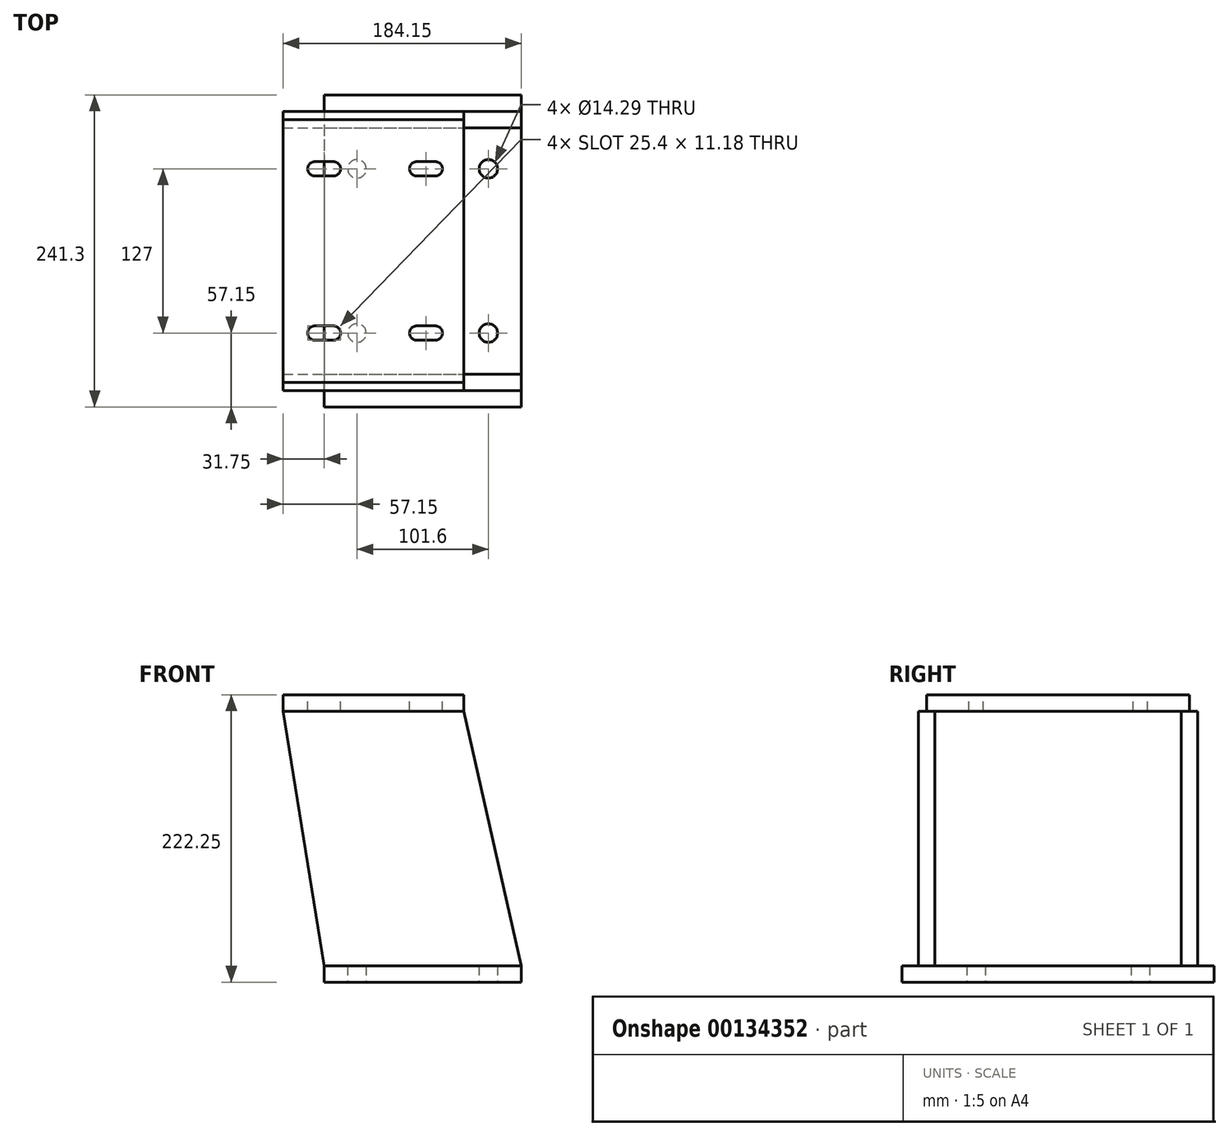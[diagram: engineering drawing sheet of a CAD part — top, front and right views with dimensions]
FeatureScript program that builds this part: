
annotation { "Feature Type Name" : "Feature", "Feature Type Description" : "" }
export const myFeature = defineFeature(function(context is Context, id is Id, definition is map)
    precondition{}
    {
        {
            var Q0;
            Q0=qCreatedBy(makeId("Top.planeOp"),FACE);
            var sketch = newSketch(context, id + "F0", { "sketchPlane" : qUnion([Q0])});
            skLineSegment(sketch, "E0.rect.bottom", {"start": v(-76.2, 120.65) * mm, "end": v(76.2, 120.65) * mm});
            skLineSegment(sketch, "E0.rect.top", {"start": v(-76.2, -120.65) * mm, "end": v(76.2, -120.65) * mm});
            skLineSegment(sketch, "E0.rect.left", {"start": v(-76.2, 120.65) * mm, "end": v(-76.2, -120.65) * mm});
            skLineSegment(sketch, "E0.rect.right", {"start": v(76.2, 120.65) * mm, "end": v(76.2, -120.65) * mm});
            skPoint(sketch, "E0.rect.middle", {"position": v(0, 0) * mm});
            skLineSegment(sketch, "E1", {"start": v(0, -142.72) * mm, "end": v(0, 120.65) * mm, "construction": true});
            skPoint(sketch, "E1.startSnap0", {"position": v(0, 120.65) * mm});
            skLineSegment(sketch, "E2", {"start": v(-76.2, 0) * mm, "end": v(76.2, 0) * mm, "construction": true});
            skLineSegment(sketch, "E3.0", {"start": v(-50.8, -142.72) * mm, "end": v(-50.8, 120.65) * mm, "construction": true});
            skLineSegment(sketch, "E4.0", {"start": v(-76.2, 63.5) * mm, "end": v(76.2, 63.5) * mm, "construction": true});
            skCircle(sketch, "E5", {"center": v(-50.8, 63.5) * mm, "radius": 7.14 * mm});
            skCircle(sketch, "E6.MirrorC", {"center": v(50.8, 63.5) * mm, "radius": 7.14 * mm});
            skCircle(sketch, "E7.MirrorC", {"center": v(-50.8, -63.5) * mm, "radius": 7.14 * mm});
            skCircle(sketch, "E8.MirrorC", {"center": v(50.8, -63.5) * mm, "radius": 7.14 * mm});
            skSolve(sketch);
        }
        {
            var Q0;
            Q0=qSketchRegion(id+"F0",true);
            extrude(context, id + "F1", {"entities" : qUnion([Q0]), "depth" : 12.7 * mm});
        }
        {
            var Q0;
            Q0=qCreatedBy(makeId("Top.planeOp"),FACE);
            cPlane(context, id + "F2", {"entities" : qUnion([Q0]), "cplaneType" : CPlaneType.OFFSET, "offset" : 222.25 * mm, "width" : 152.4 * mm, "height" : 152.4 * mm});
        }
        {
            var Q0;
            Q0=qCreatedBy(id+"F2.planeOp",FACE);
            var sketch = newSketch(context, id + "F3", { "sketchPlane" : qUnion([Q0])});
            skLineSegment(sketch, "E9.0", {"start": v(76.2, 120.65) * mm, "end": v(76.2, -120.65) * mm, "construction": true});
            skLineSegment(sketch, "E10.0", {"start": v(-107.95, 120.65) * mm, "end": v(-107.95, -120.65) * mm, "construction": true});
            skLineSegment(sketch, "E11", {"start": v(-232.66, 0) * mm, "end": v(161.6, 0) * mm, "construction": true});
            skLineSegment(sketch, "E12.0", {"start": v(-232.66, 101.6) * mm, "end": v(161.6, 101.6) * mm, "construction": true});
            skLineSegment(sketch, "E13.bottom", {"start": v(-107.95, 101.6) * mm, "end": v(31.75, 101.6) * mm});
            skLineSegment(sketch, "E13.top", {"start": v(-107.95, -101.6) * mm, "end": v(31.75, -101.6) * mm});
            skLineSegment(sketch, "E13.left", {"start": v(-107.95, 101.6) * mm, "end": v(-107.95, -101.6) * mm});
            skLineSegment(sketch, "E13.right", {"start": v(31.75, 101.6) * mm, "end": v(31.75, -101.6) * mm});
            skLineSegment(sketch, "E14", {"start": v(-35.53, 101.6) * mm, "end": v(-35.53, -101.6) * mm, "construction": true});
            skLineSegment(sketch, "E15.0", {"start": v(-232.66, 63.5) * mm, "end": v(161.6, 63.5) * mm, "construction": true});
            skLineSegment(sketch, "E16.0", {"start": v(2.57, 101.6) * mm, "end": v(2.57, -101.6) * mm, "construction": true});
            skLineSegment(sketch, "E17.0", {"start": v(-76.2, 120.65) * mm, "end": v(-76.2, -120.65) * mm, "construction": true});
            skLineSegment(sketch, "E18.0", {"start": v(-83.31, 120.65) * mm, "end": v(-83.31, -120.65) * mm, "construction": true});
            skLineSegment(sketch, "E19.0", {"start": v(-69.09, 120.65) * mm, "end": v(-69.09, -120.65) * mm, "construction": true});
            skLineSegment(sketch, "E20.0", {"start": v(9.68, 101.6) * mm, "end": v(9.68, -101.6) * mm, "construction": true});
            skLineSegment(sketch, "E21.0", {"start": v(-4.55, 101.6) * mm, "end": v(-4.55, -101.6) * mm, "construction": true});
            skLineSegment(sketch, "E22", {"start": v(-83.31, 63.5) * mm, "end": v(-69.09, 63.5) * mm});
            skLineSegment(sketch, "E23", {"start": v(-4.55, 63.5) * mm, "end": v(9.68, 63.5) * mm});
            skArc(sketch, "E24.0.startCap", {"start": v(-83.31, 57.91) * mm, "mid": v(-88.9, 63.5) * mm, "end": v(-83.31, 69.09) * mm});
            skArc(sketch, "E24.0.endCap", {"start": v(-69.09, 69.09) * mm, "mid": v(-63.5, 63.5) * mm, "end": v(-69.09, 57.91) * mm});
            skLineSegment(sketch, "E24.0.left", {"start": v(-83.31, 69.09) * mm, "end": v(-69.09, 69.09) * mm});
            skLineSegment(sketch, "E24.0.right", {"start": v(-83.31, 57.91) * mm, "end": v(-69.09, 57.91) * mm});
            skArc(sketch, "E24.1.startCap", {"start": v(-4.55, 57.91) * mm, "mid": v(-10.13, 63.5) * mm, "end": v(-4.55, 69.09) * mm});
            skArc(sketch, "E24.1.endCap", {"start": v(9.68, 69.09) * mm, "mid": v(15.27, 63.5) * mm, "end": v(9.68, 57.91) * mm});
            skLineSegment(sketch, "E24.1.left", {"start": v(-4.55, 69.09) * mm, "end": v(9.68, 69.09) * mm});
            skLineSegment(sketch, "E24.1.right", {"start": v(-4.55, 57.91) * mm, "end": v(9.68, 57.91) * mm});
            skLineSegment(sketch, "E25.MirrorCS", {"start": v(-83.31, -63.5) * mm, "end": v(-69.09, -63.5) * mm});
            skArc(sketch, "E26.MirrorCS", {"start": v(-83.31, -57.91) * mm, "mid": v(-88.9, -63.5) * mm, "end": v(-83.31, -69.09) * mm});
            skLineSegment(sketch, "E27.MirrorCS", {"start": v(-83.31, -69.09) * mm, "end": v(-69.09, -69.09) * mm});
            skArc(sketch, "E28.MirrorCS", {"start": v(-4.55, -57.91) * mm, "mid": v(-10.13, -63.5) * mm, "end": v(-4.55, -69.09) * mm});
            skArc(sketch, "E29.MirrorCS", {"start": v(9.68, -69.09) * mm, "mid": v(15.27, -63.5) * mm, "end": v(9.68, -57.91) * mm});
            skLineSegment(sketch, "E30.MirrorCS", {"start": v(-4.55, -57.91) * mm, "end": v(9.68, -57.91) * mm});
            skLineSegment(sketch, "E31.MirrorCS", {"start": v(-4.55, -63.5) * mm, "end": v(9.68, -63.5) * mm});
            skArc(sketch, "E32.MirrorCS", {"start": v(-69.09, -69.09) * mm, "mid": v(-63.5, -63.5) * mm, "end": v(-69.09, -57.91) * mm});
            skLineSegment(sketch, "E33.MirrorCS", {"start": v(-4.55, -69.09) * mm, "end": v(9.68, -69.09) * mm});
            skLineSegment(sketch, "E34.MirrorCS", {"start": v(-83.31, -57.91) * mm, "end": v(-69.09, -57.91) * mm});
            skSolve(sketch);
        }
        {
            var Q0;
            Q0=qSketchRegion(id+"F3",true);
            extrude(context, id + "F4", {"entities" : qUnion([Q0]), "oppositeDirection" : true, "depth" : 12.7 * mm});
        }
        {
            var Q0;
            Q0=qCreatedBy(makeId("Front.planeOp"),FACE);
            cPlane(context, id + "F5", {"entities" : qUnion([Q0]), "cplaneType" : CPlaneType.OFFSET, "offset" : 95.25 * mm, "width" : 152.4 * mm, "height" : 152.4 * mm});
        }
        {
            var Q0;
            Q0=qCreatedBy(id+"F5.planeOp",FACE);
            var sketch = newSketch(context, id + "F6", { "sketchPlane" : qUnion([Q0])});
            skLineSegment(sketch, "E35.0", {"start": v(-107.95, 209.55) * mm, "end": v(31.75, 209.55) * mm});
            skLineSegment(sketch, "E36.0", {"start": v(-76.2, 12.7) * mm, "end": v(76.2, 12.7) * mm});
            skLineSegment(sketch, "E37", {"start": v(31.75, 209.55) * mm, "end": v(76.2, 12.7) * mm});
            skLineSegment(sketch, "E38", {"start": v(-107.95, 209.55) * mm, "end": v(-76.2, 12.7) * mm});
            skSolve(sketch);
        }
        {
            var Q0;
            Q0=qSketchRegion(id+"F6",true);
            extrude(context, id + "F7", {"entities" : qUnion([Q0]), "depth" : 12.7 * mm});
        }
        {
            var Q0;
            Q0=makeQuery(id+"F7.opExtrude","SWEPT_BODY",BODY,{"disambiguationData":[OSD([sQuery(id+"F6.wireOp",EDGE,"E35.0"),sQuery(id+"F6.wireOp",EDGE,"E36.0"),sQuery(id+"F6.wireOp",EDGE,"E37"),sQuery(id+"F6.wireOp",EDGE,"E38")])]});
            var Q1;
            Q1=qCreatedBy(makeId("Front.planeOp"),FACE);
            mirror(context, id + "F8", {"entities" : qUnion([Q0]), "mirrorPlane" : qUnion([Q1])});
        }
    });
